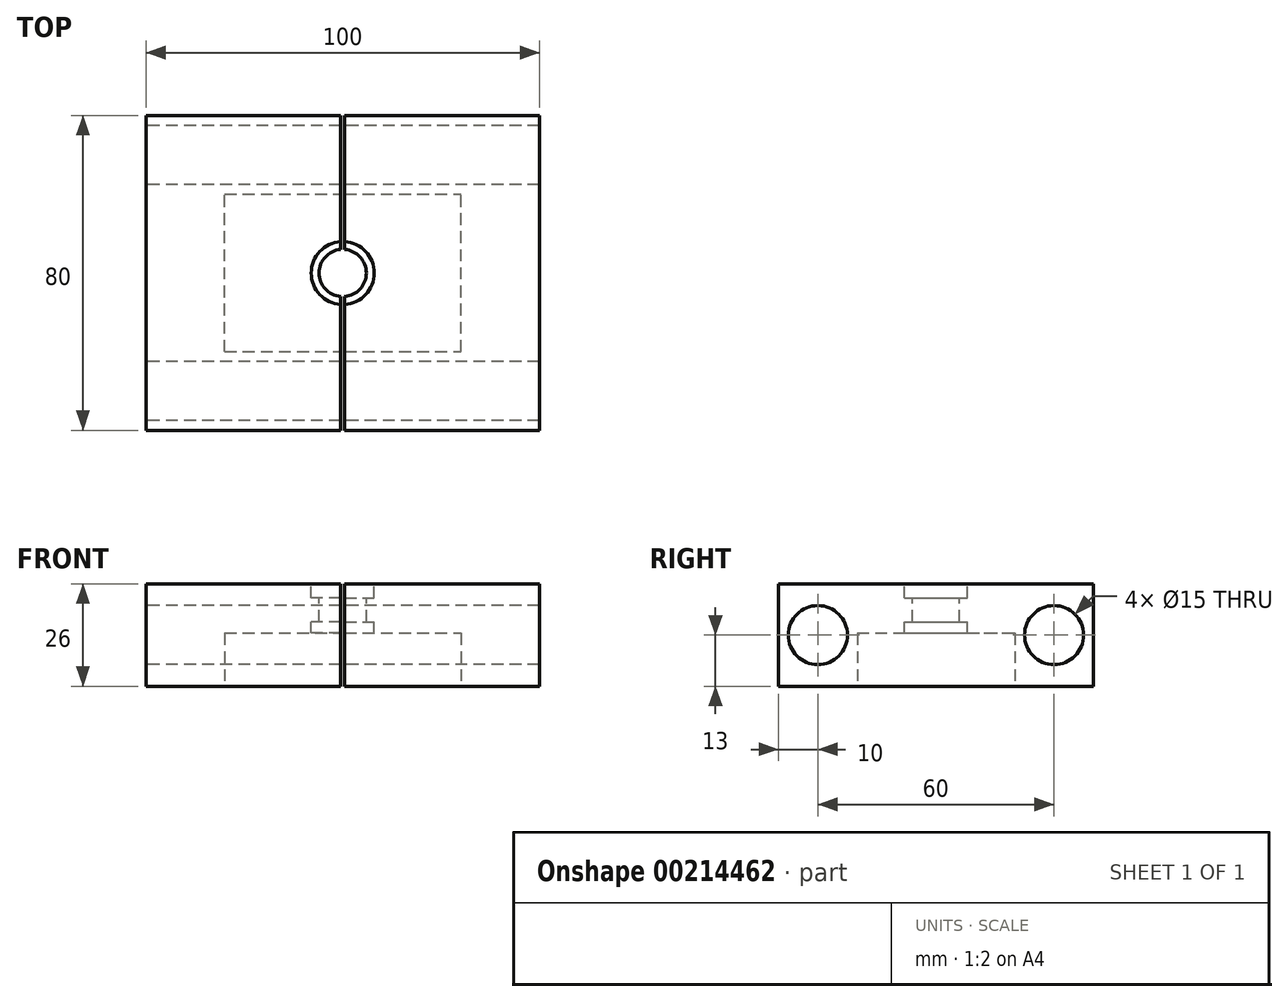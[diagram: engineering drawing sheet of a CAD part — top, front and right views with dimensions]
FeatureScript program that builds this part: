
annotation { "Feature Type Name" : "Feature", "Feature Type Description" : "" }
export const myFeature = defineFeature(function(context is Context, id is Id, definition is map)
    precondition{}
    {
        {
            var Q0;
            Q0=qCreatedBy(makeId("Right.planeOp"),FACE);
            var sketch = newSketch(context, id + "F0", { "sketchPlane" : qUnion([Q0])});
            skLineSegment(sketch, "E0.bottom", {"start": v(40, -13) * mm, "end": v(-40, -13) * mm});
            skLineSegment(sketch, "E0.top", {"start": v(40, 13) * mm, "end": v(-40, 13) * mm});
            skLineSegment(sketch, "E0.left", {"start": v(40, -13) * mm, "end": v(40, 13) * mm});
            skLineSegment(sketch, "E0.right", {"start": v(-40, -13) * mm, "end": v(-40, 13) * mm});
            skPoint(sketch, "E0.middle", {"position": v(0, 0) * mm});
            skLineSegment(sketch, "E1", {"start": v(-30, 0) * mm, "end": v(30, 0) * mm, "construction": true});
            skLineSegment(sketch, "E2", {"start": v(30, 0) * mm, "end": v(40, 0) * mm, "construction": true});
            skLineSegment(sketch, "E3", {"start": v(-30, 0) * mm, "end": v(-40, 0) * mm, "construction": true});
            skCircle(sketch, "E4", {"center": v(-30, 0) * mm, "radius": 7.5 * mm});
            skCircle(sketch, "E5", {"center": v(30, 0) * mm, "radius": 7.5 * mm});
            skSolve(sketch);
        }
        {
            var Q0;
            Q0=makeQuery(id+"F0.imprint","IMPRINT",FACE,{"disambiguationData":[TD([[makeQuery(id+"F0.imprint","IMPRINT",EDGE,{"derivedFrom":sQuery(id+"F0.wireOp",EDGE,"E0.bottom")}),-1.0]])]});
            extrude(context, id + "F1", {"entities" : qUnion([Q0]), "endBound" : BoundingType.SYMMETRIC, "depth" : 100 * mm, "offsetDistance" : 25 * mm});
        }
        {
            var Q0;
            Q0=makeQuery(id+"F1.opExtrude","SWEPT_FACE",FACE,{"disambiguationData":[OSD([sQuery(id+"F0.wireOp",EDGE,"E0.top")])]});
            var sketch = newSketch(context, id + "F2", { "sketchPlane" : qUnion([Q0])});
            skCircle(sketch, "E6", {"center": v(0, 0) * mm, "radius": 8 * mm});
            skSolve(sketch);
        }
        {
            var Q0;
            Q0=makeQuery(id+"F2.imprint","IMPRINT",FACE,{"disambiguationData":[TD([[makeQuery(id+"F2.imprint","IMPRINT",EDGE,{"derivedFrom":sQuery(id+"F2.wireOp",EDGE,"E6")}),1.0]])]});
            extrude(context, id + "F3", {"entities" : qUnion([Q0]), "operationType" : NewBodyOperationType.REMOVE, "oppositeDirection" : true, "depth" : 3.6 * mm, "offsetDistance" : 25 * mm});
        }
        {
            var Q0;
            Q0=makeQuery(id+"F3.boolean.opBoolean","COPY",FACE,{"derivedFrom":makeQuery(id+"F3.opExtrude","CAP_FACE",FACE,{"disambiguationData":[OSD([sQuery(id+"F2.wireOp",EDGE,"E6")])],"isStart":false})});
            var sketch = newSketch(context, id + "F4", { "sketchPlane" : qUnion([Q0])});
            skCircle(sketch, "E7", {"center": v(0, 0) * mm, "radius": 6 * mm});
            skSolve(sketch);
        }
        {
            var Q0;
            Q0 = qSketchRegion(id + "F4", true);
            extrude(context, id + "F5", {"entities" : qUnion([Q0]), "operationType" : NewBodyOperationType.REMOVE, "oppositeDirection" : true, "depth" : 6 * mm, "offsetDistance" : 25 * mm});
        }
        {
            var Q0;
            Q0=makeQuery(id+"F5.boolean.opBoolean","COPY",FACE,{"derivedFrom":makeQuery(id+"F5.opExtrude","CAP_FACE",FACE,{"disambiguationData":[OSD([sQuery(id+"F4.wireOp",EDGE,"E7")])],"isStart":false})});
            var sketch = newSketch(context, id + "F6", { "sketchPlane" : qUnion([Q0])});
            skCircle(sketch, "E8", {"center": v(0, 0) * mm, "radius": 8 * mm});
            skSolve(sketch);
        }
        {
            var Q0;
            Q0 = qSketchRegion(id + "F6", true);
            extrude(context, id + "F7", {"entities" : qUnion([Q0]), "operationType" : NewBodyOperationType.REMOVE, "oppositeDirection" : true, "depth" : 2.9 * mm, "offsetDistance" : 25 * mm});
        }
        {
            var Q0;
            Q0=makeQuery(id+"F1.opExtrude","SWEPT_FACE",FACE,{"disambiguationData":[OSD([sQuery(id+"F0.wireOp",EDGE,"E0.bottom")])]});
            var sketch = newSketch(context, id + "F8", { "sketchPlane" : qUnion([Q0])});
            skLineSegment(sketch, "E9.bottom", {"start": v(-30, 20) * mm, "end": v(30, 20) * mm});
            skLineSegment(sketch, "E9.top", {"start": v(-30, -20) * mm, "end": v(30, -20) * mm});
            skLineSegment(sketch, "E9.left", {"start": v(-30, 20) * mm, "end": v(-30, -20) * mm});
            skLineSegment(sketch, "E9.right", {"start": v(30, 20) * mm, "end": v(30, -20) * mm});
            skPoint(sketch, "E9.middle", {"position": v(0, 0) * mm});
            skSolve(sketch);
        }
        {
            var Q0;
            Q0 = qSketchRegion(id + "F8", true);
            var Q1;
            Q1=makeQuery(id+"F7.boolean.opBoolean","COPY",FACE,{"derivedFrom":makeQuery(id+"F7.opExtrude","CAP_FACE",FACE,{"disambiguationData":[OSD([sQuery(id+"F6.wireOp",EDGE,"E8")])],"isStart":false})});
            extrude(context, id + "F9", {"entities" : qUnion([Q0]), "operationType" : NewBodyOperationType.REMOVE, "endBound" : BoundingType.UP_TO_SURFACE, "oppositeDirection" : true, "depth" : 25 * mm, "endBoundEntityFace" : qUnion([Q1]), "offsetDistance" : 25 * mm});
        }
        {
            var Q0;
            Q0=makeQuery(id+"F1.opExtrude","SWEPT_FACE",FACE,{"disambiguationData":[OSD([sQuery(id+"F0.wireOp",EDGE,"E0.top")])]});
            var sketch = newSketch(context, id + "F10", { "sketchPlane" : qUnion([Q0])});
            skLineSegment(sketch, "E10.bottom", {"start": v(0.5, -40) * mm, "end": v(-0.5, -40) * mm});
            skLineSegment(sketch, "E10.top", {"start": v(0.5, 40) * mm, "end": v(-0.5, 40) * mm});
            skLineSegment(sketch, "E10.left", {"start": v(0.5, -40) * mm, "end": v(0.5, 40) * mm});
            skLineSegment(sketch, "E10.right", {"start": v(-0.5, -40) * mm, "end": v(-0.5, 40) * mm});
            skPoint(sketch, "E10.middle", {"position": v(0, 0) * mm});
            skSolve(sketch);
        }
        {
            var Q0;
            {var subQ0=sQuery(id+"F10.wireOp",EDGE,"E10.bottom");Q0=makeQuery(id+"F10.imprint","IMPRINT",FACE,{"disambiguationData":[TD([[makeQuery(id+"F10.imprint","IMPRINT",EDGE,{"derivedFrom":subQ0}),-1.0]])]});}
            var Q1;
            {var subQ0=sQuery(id+"F10.wireOp",EDGE,"E10.left");var subQ1=makeQuery(id+"F3.boolean.opBoolean","COPY",EDGE,{"derivedFrom":makeQuery(id+"F3.opExtrude","CAP_EDGE",EDGE,{"disambiguationData":[OSD([sQuery(id+"F2.wireOp",EDGE,"E6")])],"isStart":true})});var subQ2=makeQuery(id+"F10.imprint","INTERSECT",VERTEX,{"disambiguationData":[OD(0.0)],"derivedFrom":[subQ1,subQ0]});Q1=makeQuery(id+"F10.imprint","IMPRINT",FACE,{"disambiguationData":[TD([[makeQuery(id+"F10.imprint","IMPRINT",EDGE,{"disambiguationData":[TD([[subQ2,-1.0]])],"derivedFrom":subQ0}),1.0]])]});}
            var Q2;
            {var subQ0=sQuery(id+"F10.wireOp",EDGE,"E10.top");Q2=makeQuery(id+"F10.imprint","IMPRINT",FACE,{"disambiguationData":[TD([[makeQuery(id+"F10.imprint","IMPRINT",EDGE,{"derivedFrom":subQ0}),1.0]])]});}
            var Q3;
            Q3=makeQuery(id+"F1.opExtrude","SWEPT_FACE",FACE,{"disambiguationData":[OSD([sQuery(id+"F0.wireOp",EDGE,"E0.bottom")])]});
            extrude(context, id + "F11", {"entities" : qUnion([Q0, Q1, Q2]), "operationType" : NewBodyOperationType.REMOVE, "endBound" : BoundingType.UP_TO_SURFACE, "oppositeDirection" : true, "depth" : 25 * mm, "endBoundEntityFace" : qUnion([Q3]), "offsetDistance" : 25 * mm});
        }
    });
